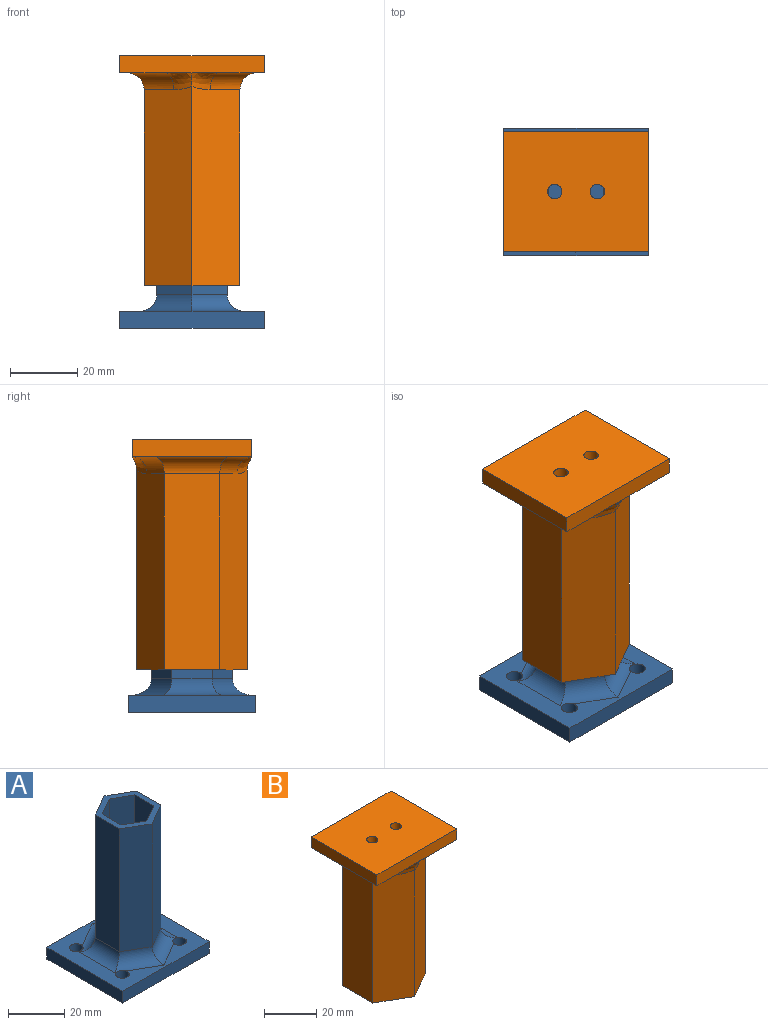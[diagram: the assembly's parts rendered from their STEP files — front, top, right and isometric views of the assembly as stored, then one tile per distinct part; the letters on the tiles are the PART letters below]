
ASSEMBLY  parts=2 mates=1
PART A: 30 faces, bbox 43.2x38.1x63.5 mm
  f0: plane 43.18x38.1mm, normal (0,0,1), area 744mm2, adj f2,f3,f4,f5,f6,f7,f22,f23
  f1: plane 43.18x38.1mm, normal (0,0,-1), area 1572mm2, adj f4,f5,f6,f7,f26,f27,f28,f29
  f2: cylinder r=5.08mm len=18.07mm, axis (-0.87,-0.5,0), area 111.4mm2, adj f0,f14,f22,f24,f29
  f3: cylinder r=5.08mm len=18.07mm, axis (0.87,0.5,0), area 111.4mm2, adj f0,f17,f23,f25,f26
  f4: plane 38.1x5.08mm, normal (-1,0,0), area 193.5mm2, adj f0,f1,f6,f7
  f5: plane 38.1x5.08mm, normal (1,0,0), area 193.5mm2, adj f0,f1,f6,f7
  f6: plane 43.18x5.08mm, normal (0,-1,0), area 219.4mm2, adj f0,f1,f4,f5
  f7: plane 43.18x5.08mm, normal (0,1,0), area 219.4mm2, adj f0,f1,f4,f5
  f8: plane 58.42x8.25mm, normal (0.5,-0.87,0), area 556.5mm2, adj f9,f19,f20,f21
  f9: plane 58.42x8.25mm, normal (-0.5,-0.87,0), area 556.5mm2, adj f8,f10,f20,f21
  f10: plane 58.42x9.53mm, normal (-1,0,0), area 556.5mm2, adj f9,f11,f20,f21
  f11: plane 58.42x8.25mm, normal (-0.5,0.87,0), area 556.5mm2, adj f10,f12,f20,f21
  f12: plane 58.42x8.25mm, normal (0.5,0.87,0), area 556.5mm2, adj f11,f19,f20,f21
  f13: plane 53.34x10.45mm, normal (0.5,0.87,0), area 643.5mm2, adj f14,f18,f20,f24
  f14: plane 53.34x10.45mm, normal (-0.5,0.87,0), area 643.5mm2, adj f2,f13,f15,f20
  f15: plane 53.34x12.07mm, normal (-1,0,0), area 643.5mm2, adj f14,f16,f20,f22
  f16: plane 53.34x10.45mm, normal (-0.5,-0.87,0), area 643.5mm2, adj f15,f17,f20,f23
  f17: plane 53.34x10.45mm, normal (0.5,-0.87,0), area 643.5mm2, adj f3,f16,f18,f20
  f18: plane 53.34x12.07mm, normal (1,0,0), area 643.5mm2, adj f13,f17,f20,f25
  f19: plane 58.42x9.53mm, normal (1,0,0), area 556.5mm2, adj f8,f12,f20,f21
  f20: plane 24.13x20.9mm, normal (0,0,1), area 142.5mm2, adj f8,f9,f10,f11,f12,f13,f14,f15
  f21: plane 19.05x16.5mm, normal (0,0,1), area 235.7mm2, adj f8,f9,f10,f11,f12,f19
  f22: cylinder r=5.08mm len=17.93mm, axis (0,-1,0), area 113.3mm2, adj f0,f2,f15,f23
  f23: cylinder r=5.08mm len=18.07mm, axis (0.87,-0.5,0), area 111.4mm2, adj f0,f3,f16,f22,f28
  f24: cylinder r=5.08mm len=18.07mm, axis (-0.87,0.5,0), area 111.4mm2, adj f0,f2,f13,f25,f27
  f25: cylinder r=5.08mm len=17.93mm, axis (0,1,0), area 113.3mm2, adj f0,f3,f18,f24
  f26: cylinder r=2.41mm len=5.14mm, axis (0,0,-1), area 77.1mm2, adj f0,f1,f3
  f27: cylinder r=2.41mm len=5.14mm, axis (0,0,-1), area 77.1mm2, adj f0,f1,f24
  f28: cylinder r=2.41mm len=5.14mm, axis (0,0,-1), area 77.1mm2, adj f0,f1,f23
  f29: cylinder r=2.41mm len=5.14mm, axis (0,0,-1), area 77.1mm2, adj f0,f1,f2
PART B: 47 faces, bbox 45.4x38.6x70.8 mm
  f0: cylinder r=2.16mm len=12.7mm, axis (0,0,1), area 172.3mm2, adj f5,f46
  f1: cylinder r=2.16mm len=12.7mm, axis (0,0,1), area 172.3mm2, adj f5,f39
  f2: plane 27.94x24.2mm, normal (0,0,-1), area 359.2mm2, adj f10,f11,f12,f13,f14,f21,f33,f34
  f3: plane 35.56x13.63mm, normal (0,0,-1), area 153.9mm2, adj f7,f8,f9,f27,f29,f31
  f4: plane 35.56x13.63mm, normal (0,0,-1), area 153.9mm2, adj f6,f8,f9,f24,f26,f28
  f5: plane 43.18x35.56mm, normal (0,0,1), area 1506.2mm2, adj f0,f1,f6,f7,f8,f9
  f6: plane 35.56x5.08mm, normal (-1,0,0), area 180.6mm2, adj f4,f5,f8,f9
  f7: plane 35.56x5.08mm, normal (1,0,0), area 180.6mm2, adj f3,f5,f8,f9
  f8: plane 45.39x7.29mm, normal (0,-1,0), area 219.4mm2, adj f3,f4,f5,f6,f7,f30,f32
  f9: plane 44.48x6.38mm, normal (0,1,0), area 219.4mm2, adj f3,f4,f5,f6,f7,f23,f25
  f10: plane 50.8x13.97mm, normal (1,0,0), area 709.7mm2, adj f2,f11,f21,f22
  f11: plane 50.8x12.1mm, normal (0.5,0.87,0), area 709.7mm2, adj f2,f10,f12,f22
  f12: plane 50.8x12.1mm, normal (-0.5,0.87,0), area 709.7mm2, adj f2,f11,f13,f22
  f13: plane 50.8x13.97mm, normal (-1,0,0), area 709.7mm2, adj f2,f12,f14,f22
  f14: plane 50.8x12.1mm, normal (-0.5,-0.87,0), area 709.7mm2, adj f2,f13,f21,f22
  f15: plane 59.5x14.3mm, normal (-0.5,-0.87,0), area 966.7mm2, adj f16,f20,f22,f28,f30
  f16: plane 58.42x16.51mm, normal (-1,0,0), area 964.5mm2, adj f15,f17,f22,f26
  f17: plane 59.5x14.3mm, normal (-0.5,0.87,0), area 966.7mm2, adj f16,f18,f22,f23,f24
  f18: plane 59.5x14.3mm, normal (0.5,0.87,0), area 966.7mm2, adj f17,f19,f22,f25,f27
  f19: plane 58.42x16.51mm, normal (1,0,0), area 964.5mm2, adj f18,f20,f22,f29
  f20: plane 59.5x14.3mm, normal (0.5,-0.87,0), area 966.7mm2, adj f15,f19,f22,f31,f32
  f21: plane 50.8x12.1mm, normal (0.5,-0.87,0), area 709.7mm2, adj f2,f10,f14,f22
  f22: plane 33.02x28.6mm, normal (0,0,-1), area 201.1mm2, adj f10,f11,f12,f13,f14,f15,f16,f17
  f23: bspline ~11.52x5.39mm, area 41.1mm2, adj f9,f17,f24,f25
  f24: cylinder r=5.08mm len=13.96mm, axis (0.87,0.5,0), area 93.5mm2, adj f4,f17,f23,f26
  f25: bspline ~11.13x5.22mm, area 41.1mm2, adj f9,f18,f23,f27
  f26: cylinder r=5.08mm len=22.38mm, axis (0,1,0), area 155.1mm2, adj f4,f16,f24,f28
  f27: cylinder r=5.08mm len=13.96mm, axis (0.87,-0.5,0), area 93.5mm2, adj f3,f18,f25,f29
  f28: cylinder r=5.08mm len=13.96mm, axis (-0.87,0.5,0), area 93.5mm2, adj f4,f15,f26,f30
  f29: cylinder r=5.08mm len=22.38mm, axis (0,-1,0), area 155.1mm2, adj f3,f19,f27,f31
  f30: bspline ~11.79x5.54mm, area 41.3mm2, adj f8,f15,f28,f32
  f31: cylinder r=5.08mm len=13.96mm, axis (-0.87,-0.5,0), area 93.5mm2, adj f3,f20,f29,f32
  f32: bspline ~11.83x5.51mm, area 41.3mm2, adj f8,f20,f30,f31
  f33: plane 5.08x4.62mm, normal (0.87,0.5,0), area 27.1mm2, adj f2,f34,f38,f39
  f34: plane 5.08x4.62mm, normal (0.87,-0.5,0), area 27.1mm2, adj f2,f33,f35,f39
  f35: plane 5.33x5.08mm, normal (0,-1,0), area 27.1mm2, adj f2,f34,f36,f39
  f36: plane 5.08x4.62mm, normal (-0.87,-0.5,0), area 27.1mm2, adj f2,f35,f37,f39
  f37: plane 5.08x4.62mm, normal (-0.87,0.5,0), area 27.1mm2, adj f2,f36,f38,f39
  f38: plane 5.33x5.08mm, normal (0,1,0), area 27.1mm2, adj f2,f33,f37,f39
  f39: plane 10.67x9.24mm, normal (0,0,-1), area 59.3mm2, adj f1,f33,f34,f35,f36,f37,f38
  f40: plane 5.08x4.62mm, normal (0.87,0.5,0), area 27.1mm2, adj f2,f41,f45,f46
  f41: plane 5.08x4.62mm, normal (0.87,-0.5,0), area 27.1mm2, adj f2,f40,f42,f46
  f42: plane 5.33x5.08mm, normal (0,-1,0), area 27.1mm2, adj f2,f41,f43,f46
  f43: plane 5.08x4.62mm, normal (-0.87,-0.5,0), area 27.1mm2, adj f2,f42,f44,f46
  f44: plane 5.08x4.62mm, normal (-0.87,0.5,0), area 27.1mm2, adj f2,f43,f45,f46
  f45: plane 5.33x5.08mm, normal (0,1,0), area 27.1mm2, adj f2,f40,f44,f46
  f46: plane 10.67x9.24mm, normal (0,0,-1), area 59.3mm2, adj f0,f40,f41,f42,f43,f44,f45
PLACE A t=(-145.47,-117.29,-230.6)mm
PLACE B t=(-145.47,-117.29,-199.47)mm
MATE slider B.f2 <-> A.f20  axis (0,0,-1) through (-145.47,-117.29,-183.43)mm
